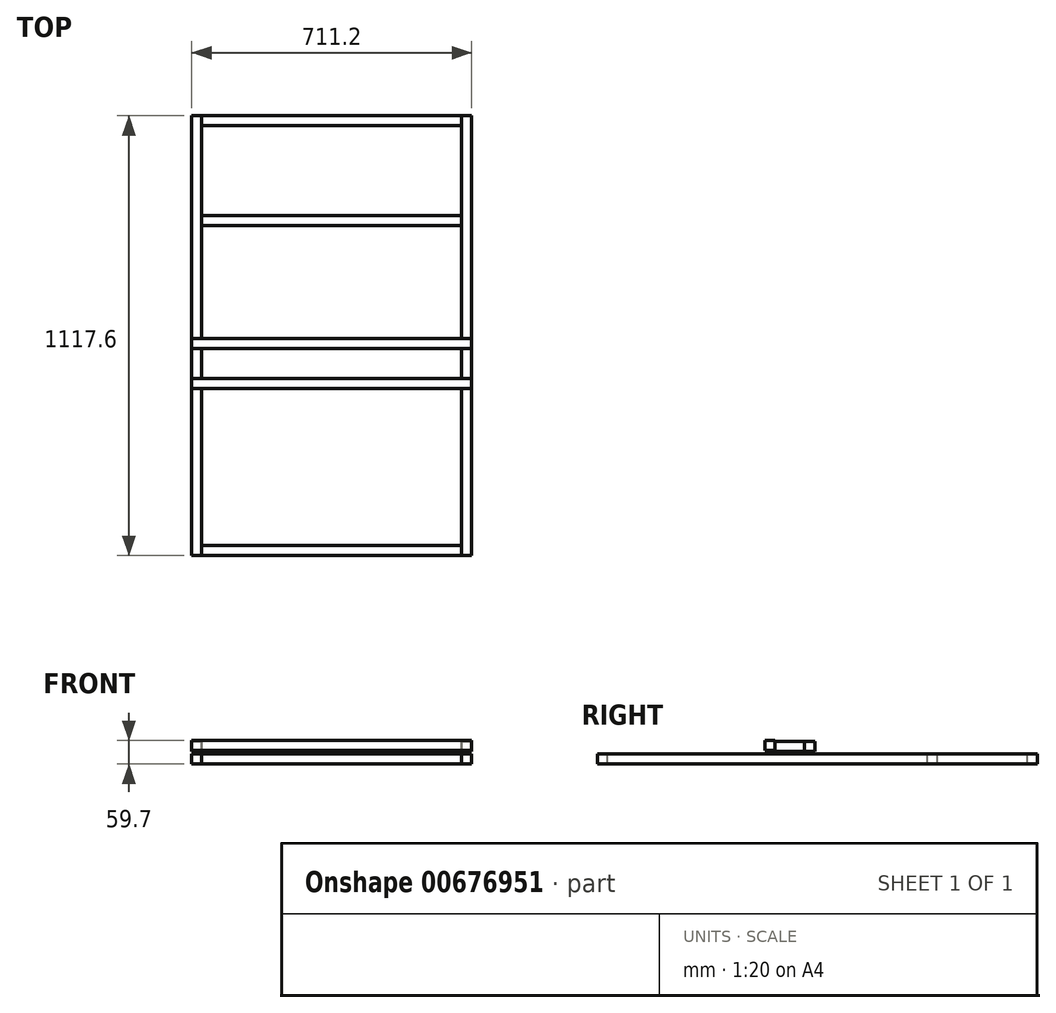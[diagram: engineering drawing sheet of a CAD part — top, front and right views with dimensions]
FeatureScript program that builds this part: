
annotation { "Feature Type Name" : "Feature", "Feature Type Description" : "" }
export const myFeature = defineFeature(function(context is Context, id is Id, definition is map)
    precondition{}
    {
        {
            var Q0;
            Q0=qCreatedBy(makeId("Front.planeOp"),FACE);
            var sketch = newSketch(context, id + "F0", { "sketchPlane" : qUnion([Q0])});
            skLineSegment(sketch, "E0.bottom", {"start": v(-330.2, -12.7) * mm, "end": v(-355.6, -12.7) * mm});
            skLineSegment(sketch, "E0.top", {"start": v(-330.2, 12.7) * mm, "end": v(-355.6, 12.7) * mm});
            skLineSegment(sketch, "E0.left", {"start": v(-330.2, -12.7) * mm, "end": v(-330.2, 12.7) * mm});
            skLineSegment(sketch, "E0.right", {"start": v(-355.6, -12.7) * mm, "end": v(-355.6, 12.7) * mm});
            skPoint(sketch, "E0.middle", {"position": v(-342.9, 0) * mm});
            skLineSegment(sketch, "E1.bottom", {"start": v(355.6, -12.7) * mm, "end": v(330.2, -12.7) * mm});
            skLineSegment(sketch, "E1.top", {"start": v(355.6, 12.7) * mm, "end": v(330.2, 12.7) * mm});
            skLineSegment(sketch, "E1.left", {"start": v(355.6, -12.7) * mm, "end": v(355.6, 12.7) * mm});
            skLineSegment(sketch, "E1.right", {"start": v(330.2, -12.7) * mm, "end": v(330.2, 12.7) * mm});
            skPoint(sketch, "E1.middle", {"position": v(342.9, 0) * mm});
            skLineSegment(sketch, "E2", {"start": v(-342.9, 0) * mm, "end": v(342.9, 0) * mm, "construction": true});
            skSolve(sketch);
        }
        {
            var Q0;
            Q0 = qSketchRegion(id + "F0", true);
            extrude(context, id + "F1", {"entities" : qUnion([Q0]), "endBound" : BoundingType.SYMMETRIC, "depth" : 1117.6 * mm, "offsetDistance" : 25.4 * mm});
        }
        {
            var Q0;
            Q0=makeQuery(id+"F1.opExtrude","SWEPT_FACE",FACE,{"disambiguationData":[OSD([sQuery(id+"F0.wireOp",EDGE,"E0.left")])]});
            var sketch = newSketch(context, id + "F2", { "sketchPlane" : qUnion([Q0])});
            skLineSegment(sketch, "E3.bottom", {"start": v(558.8, 12.7) * mm, "end": v(533.4, 12.7) * mm});
            skLineSegment(sketch, "E3.top", {"start": v(558.8, -12.7) * mm, "end": v(533.4, -12.7) * mm});
            skLineSegment(sketch, "E3.left", {"start": v(558.8, 12.7) * mm, "end": v(558.8, -12.7) * mm});
            skLineSegment(sketch, "E3.right", {"start": v(533.4, 12.7) * mm, "end": v(533.4, -12.7) * mm});
            skLineSegment(sketch, "E4.bottom", {"start": v(304.8, 12.7) * mm, "end": v(279.4, 12.7) * mm});
            skLineSegment(sketch, "E4.top", {"start": v(304.8, -12.7) * mm, "end": v(279.4, -12.7) * mm});
            skLineSegment(sketch, "E4.left", {"start": v(304.8, 12.7) * mm, "end": v(304.8, -12.7) * mm});
            skLineSegment(sketch, "E4.right", {"start": v(279.4, 12.7) * mm, "end": v(279.4, -12.7) * mm});
            skLineSegment(sketch, "E5.bottom", {"start": v(-558.8, 12.7) * mm, "end": v(-533.4, 12.7) * mm});
            skLineSegment(sketch, "E5.top", {"start": v(-558.8, -12.7) * mm, "end": v(-533.4, -12.7) * mm});
            skLineSegment(sketch, "E5.left", {"start": v(-558.8, 12.7) * mm, "end": v(-558.8, -12.7) * mm});
            skLineSegment(sketch, "E5.right", {"start": v(-533.4, 12.7) * mm, "end": v(-533.4, -12.7) * mm});
            skSolve(sketch);
        }
        {
            var Q0;
            Q0 = qSketchRegion(id + "F2", true);
            extrude(context, id + "F3", {"entities" : qUnion([Q0]), "endBound" : BoundingType.UP_TO_NEXT, "depth" : 25.4 * mm, "offsetDistance" : 25.4 * mm});
        }
        {
            var Q0;
            Q0=makeQuery(id+"F1.opExtrude","SWEPT_FACE",FACE,{"disambiguationData":[OSD([sQuery(id+"F0.wireOp",EDGE,"E0.right")])]});
            var sketch = newSketch(context, id + "F4", { "sketchPlane" : qUnion([Q0])});
            skLineSegment(sketch, "E6.bottom", {"start": v(7.57, 44.45) * mm, "end": v(32.97, 44.45) * mm});
            skLineSegment(sketch, "E6.top", {"start": v(7.57, 19.05) * mm, "end": v(32.97, 19.05) * mm});
            skLineSegment(sketch, "E6.left", {"start": v(7.57, 44.45) * mm, "end": v(7.57, 19.05) * mm});
            skLineSegment(sketch, "E6.right", {"start": v(32.97, 44.45) * mm, "end": v(32.97, 19.05) * mm});
            skLineSegment(sketch, "E7.bottom", {"start": v(109.17, 47) * mm, "end": v(134.57, 47) * mm});
            skLineSegment(sketch, "E7.top", {"start": v(109.17, 21.6) * mm, "end": v(134.57, 21.6) * mm});
            skLineSegment(sketch, "E7.left", {"start": v(109.17, 47) * mm, "end": v(109.17, 21.6) * mm});
            skLineSegment(sketch, "E7.right", {"start": v(134.57, 47) * mm, "end": v(134.57, 21.6) * mm});
            skSolve(sketch);
        }
        {
            var Q0;
            Q0 = qSketchRegion(id + "F4", true);
            var Q1;
            Q1=makeQuery(id+"F1.opExtrude","SWEPT_FACE",FACE,{"disambiguationData":[OSD([sQuery(id+"F0.wireOp",EDGE,"E1.left")])]});
            extrude(context, id + "F5", {"entities" : qUnion([Q0]), "endBound" : BoundingType.UP_TO_SURFACE, "oppositeDirection" : true, "depth" : 25.4 * mm, "endBoundEntityFace" : qUnion([Q1]), "offsetDistance" : 25.4 * mm});
        }
        {
            var Q0;
            Q0=makeQuery(id+"F5.opExtrude","SWEPT_FACE",FACE,{"disambiguationData":[OSD([sQuery(id+"F4.wireOp",EDGE,"E6.right")])]});
            var sketch = newSketch(context, id + "F6", { "sketchPlane" : qUnion([Q0])});
            skLineSegment(sketch, "E8.bottom", {"start": v(-355.6, 44.45) * mm, "end": v(-330.2, 44.45) * mm});
            skLineSegment(sketch, "E8.top", {"start": v(-355.6, 19.05) * mm, "end": v(-330.2, 19.05) * mm});
            skLineSegment(sketch, "E8.left", {"start": v(-355.6, 44.45) * mm, "end": v(-355.6, 19.05) * mm});
            skLineSegment(sketch, "E8.right", {"start": v(-330.2, 44.45) * mm, "end": v(-330.2, 19.05) * mm});
            skLineSegment(sketch, "E9.bottom", {"start": v(355.6, 44.45) * mm, "end": v(330.2, 44.45) * mm});
            skLineSegment(sketch, "E9.top", {"start": v(355.6, 19.05) * mm, "end": v(330.2, 19.05) * mm});
            skLineSegment(sketch, "E9.left", {"start": v(355.6, 44.45) * mm, "end": v(355.6, 19.05) * mm});
            skLineSegment(sketch, "E9.right", {"start": v(330.2, 44.45) * mm, "end": v(330.2, 19.05) * mm});
            skSolve(sketch);
        }
        {
            var Q0;
            Q0 = qSketchRegion(id + "F6", true);
            var Q1;
            Q1=makeQuery(id+"F5.opExtrude","SWEPT_FACE",FACE,{"disambiguationData":[OSD([sQuery(id+"F4.wireOp",EDGE,"E7.left")])]});
            extrude(context, id + "F7", {"entities" : qUnion([Q0]), "endBound" : BoundingType.UP_TO_SURFACE, "depth" : 25.4 * mm, "endBoundEntityFace" : qUnion([Q1]), "offsetDistance" : 25.4 * mm});
        }
    });
